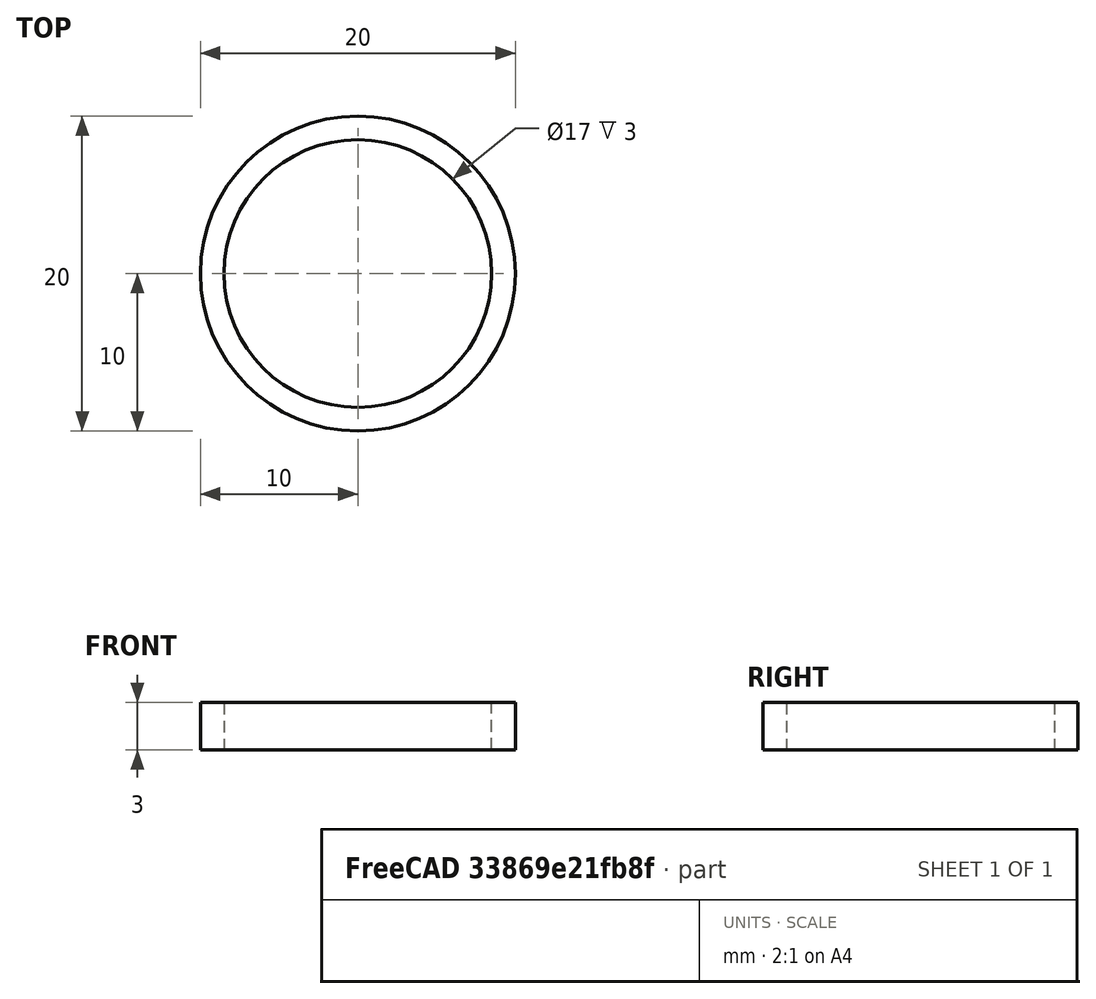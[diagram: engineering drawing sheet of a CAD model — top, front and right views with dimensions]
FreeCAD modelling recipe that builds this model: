
FCSTD DOCUMENT  (FreeCAD 1.0R39285 (Git))
Label: encoder_fit_test
License: All rights reserved
LicenseURL: https://en.wikipedia.org/wiki/All_rights_reserved
objects: Sketcher::SketchObject×1, PartDesign::Pad×1, PartDesign::Body×1
note: 6 computed .brp shape members not serialized (recipe doc carries the construction recipe); baked Part::Feature solids carry a one-line shape summary decoded from their .brp

FEATURE [Sketcher::SketchObject] Sketch
  ArcFitTolerance = 1e-06
  AttachmentSupport = -> [XY_Plane]
  FullyConstrained = true
  MakeInternals = false
  MapMode = 5
  sketch-geometry (2):
    g0: Circle CenterX=0 CenterY=0 CenterZ=0 NormalX=0 NormalY=0 NormalZ=1 AngleXU=0 Radius=8.5
    g1: Circle CenterX=0 CenterY=0 CenterZ=0 NormalX=0 NormalY=0 NormalZ=1 AngleXU=0 Radius=10
  constraints (4):
    c: Coincident(g0,g-1)
    c: Coincident(g1,g0)
    c: Diameter(g0) = 17
    c: Diameter(g1) = 20
FEATURE [PartDesign::Pad] Pad
  Direction = (0,0,1)
  Length = 3
  Length2 = 10
  Profile = -> Sketch
  ReferenceAxis = -> Sketch [N_Axis]
  Refine = true
  Suppressed = false
  Type = 0
FEATURE [PartDesign::Body] Body
  AllowCompound = false
  Group = -> [Sketch,Pad]
  Origin = -> Origin
  Tip = -> Pad
